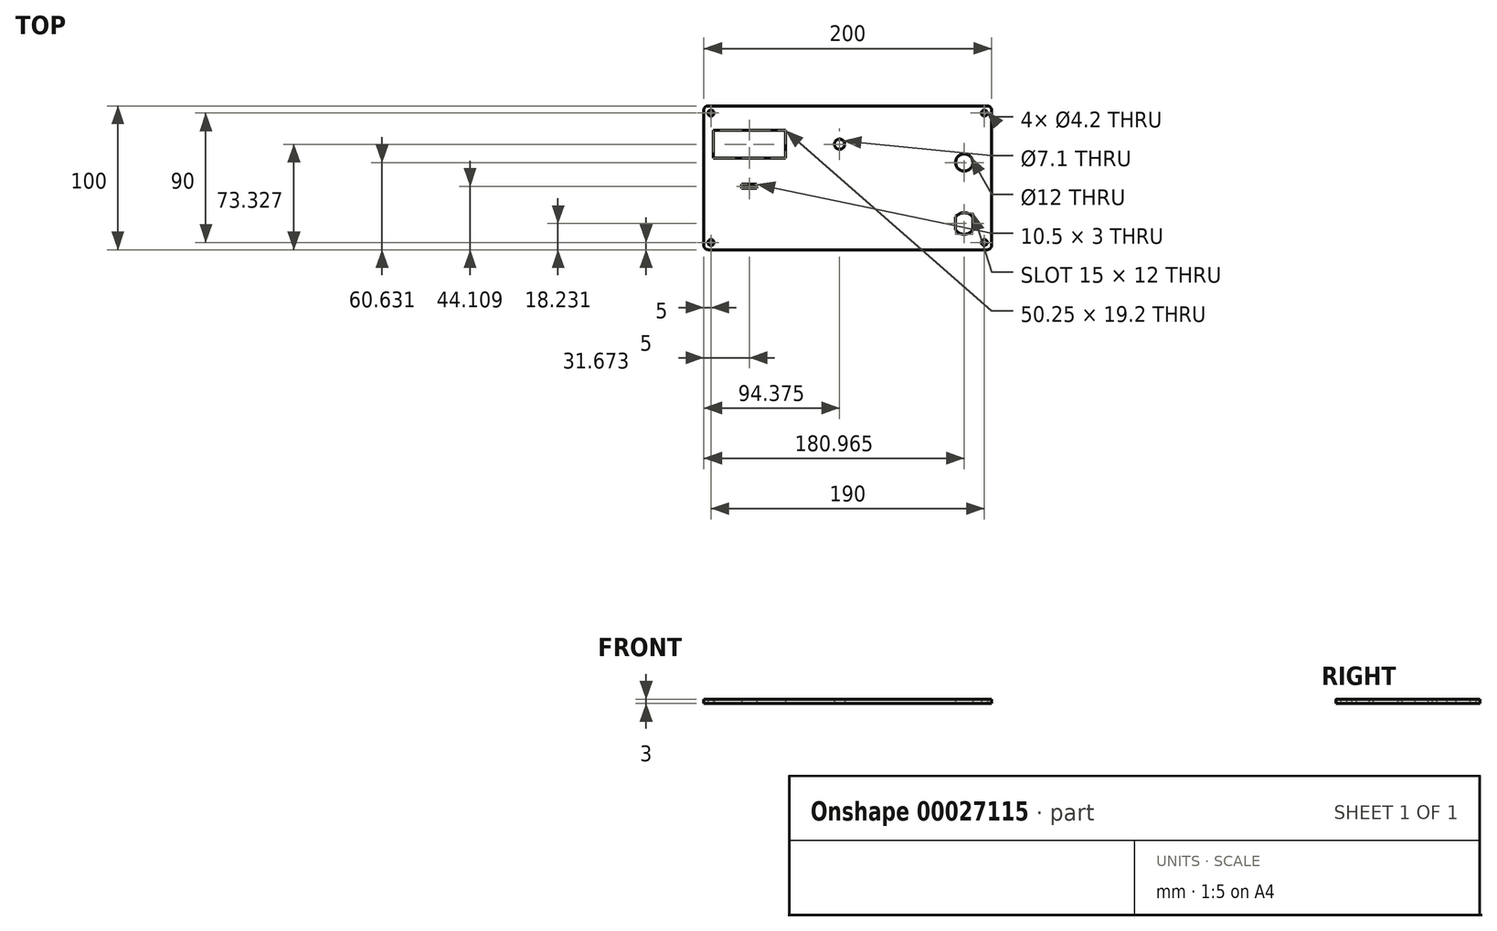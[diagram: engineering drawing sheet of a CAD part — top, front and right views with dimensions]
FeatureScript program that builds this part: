
annotation { "Feature Type Name" : "Feature", "Feature Type Description" : "" }
export const myFeature = defineFeature(function(context is Context, id is Id, definition is map)
    precondition{}
    {
        {
            var Q0;
            Q0=qCreatedBy(makeId("Top.planeOp"),FACE);
            var sketch = newSketch(context, id + "F0", { "sketchPlane" : qUnion([Q0])});
            skLineSegment(sketch, "E0.rect.bottom", {"start": v(100, -50) * mm, "end": v(-100, -50) * mm});
            skLineSegment(sketch, "E0.rect.top", {"start": v(100, 50) * mm, "end": v(-100, 50) * mm});
            skLineSegment(sketch, "E0.rect.left", {"start": v(100, -50) * mm, "end": v(100, 50) * mm});
            skLineSegment(sketch, "E0.rect.right", {"start": v(-100, -50) * mm, "end": v(-100, 50) * mm});
            skPoint(sketch, "E0.rect.middle", {"position": v(0, 0) * mm});
            skLineSegment(sketch, "E1.0", {"start": v(95, 45) * mm, "end": v(-95, 45) * mm, "construction": true});
            skLineSegment(sketch, "E1.1", {"start": v(95, -45) * mm, "end": v(95, 45) * mm, "construction": true});
            skLineSegment(sketch, "E1.2", {"start": v(95, -45) * mm, "end": v(-95, -45) * mm, "construction": true});
            skLineSegment(sketch, "E1.3", {"start": v(-95, -45) * mm, "end": v(-95, 45) * mm, "construction": true});
            skCircle(sketch, "E2", {"center": v(-95, 45) * mm, "radius": 2.1 * mm});
            skCircle(sketch, "E3.MirrorC", {"center": v(95, -45) * mm, "radius": 2.1 * mm});
            skLineSegment(sketch, "E4.bottom", {"start": v(-93.45, 32.93) * mm, "end": v(-43.2, 32.93) * mm});
            skLineSegment(sketch, "E4.top", {"start": v(-93.45, 13.73) * mm, "end": v(-43.2, 13.73) * mm});
            skLineSegment(sketch, "E4.left", {"start": v(-93.45, 32.93) * mm, "end": v(-93.45, 13.73) * mm});
            skLineSegment(sketch, "E4.right", {"start": v(-43.2, 32.93) * mm, "end": v(-43.2, 13.73) * mm});
            skLineSegment(sketch, "E5", {"start": v(-68.33, 32.93) * mm, "end": v(-68.33, 13.73) * mm, "construction": true});
            skLineSegment(sketch, "E6", {"start": v(-93.45, 23.33) * mm, "end": v(-43.2, 23.33) * mm, "construction": true});
            skLineSegment(sketch, "E7.rect.bottom", {"start": v(-43.2, 36.83) * mm, "end": v(-93.45, 36.83) * mm, "construction": true});
            skLineSegment(sketch, "E7.rect.top", {"start": v(-43.2, 9.83) * mm, "end": v(-93.45, 9.83) * mm, "construction": true});
            skLineSegment(sketch, "E7.rect.left", {"start": v(-43.2, 36.83) * mm, "end": v(-43.2, 9.83) * mm, "construction": true});
            skLineSegment(sketch, "E7.rect.right", {"start": v(-93.45, 36.83) * mm, "end": v(-93.45, 9.83) * mm, "construction": true});
            skPoint(sketch, "E7.rect.middle", {"position": v(-68.33, 23.33) * mm});
            skLineSegment(sketch, "E8.rect.bottom", {"start": v(-50.43, -4.4) * mm, "end": v(-86.23, -4.4) * mm, "construction": true});
            skLineSegment(sketch, "E8.rect.top", {"start": v(-50.43, -36.4) * mm, "end": v(-86.23, -36.4) * mm, "construction": true});
            skLineSegment(sketch, "E8.rect.left", {"start": v(-50.43, -4.4) * mm, "end": v(-50.43, -36.4) * mm, "construction": true});
            skLineSegment(sketch, "E8.rect.right", {"start": v(-86.23, -4.4) * mm, "end": v(-86.23, -36.4) * mm, "construction": true});
            skPoint(sketch, "E8.rect.middle", {"position": v(-68.33, -20.4) * mm});
            skLineSegment(sketch, "E9.rect.bottom", {"start": v(-63.08, -7.4) * mm, "end": v(-73.58, -7.4) * mm});
            skLineSegment(sketch, "E9.rect.left", {"start": v(-63.08, -7.4) * mm, "end": v(-63.08, -4.4) * mm});
            skLineSegment(sketch, "E9.rect.right", {"start": v(-73.58, -7.4) * mm, "end": v(-73.58, -4.4) * mm});
            skPoint(sketch, "E9.rect.middle", {"position": v(-68.33, -4.4) * mm});
            skLineSegment(sketch, "E10", {"start": v(-73.58, -4.4) * mm, "end": v(-63.08, -4.4) * mm});
            skPoint(sketch, "E11.orphan", {"position": v(-63.08, -1.4) * mm});
            skPoint(sketch, "E12.orphan", {"position": v(-73.58, -1.4) * mm});
            skCircle(sketch, "E13", {"center": v(-5.63, 23.33) * mm, "radius": 3.55 * mm});
            skCircle(sketch, "E14", {"center": v(-5.63, 23.33) * mm, "radius": 9.25 * mm, "construction": true});
            skArc(sketch, "E15", {"start": v(74.97, -36.27) * mm, "mid": v(80.97, -39.27) * mm, "end": v(86.97, -36.27) * mm});
            skLineSegment(sketch, "E16", {"start": v(86.97, -27.27) * mm, "end": v(86.97, -36.27) * mm});
            skLineSegment(sketch, "E17", {"start": v(80.97, -24.27) * mm, "end": v(80.97, -39.27) * mm, "construction": true});
            skLineSegment(sketch, "E18.MirrorCS", {"start": v(74.97, -27.27) * mm, "end": v(74.97, -36.27) * mm});
            skArc(sketch, "E19.trimOffspring", {"start": v(86.97, -27.27) * mm, "mid": v(80.97, -24.27) * mm, "end": v(74.97, -27.27) * mm});
            skLineSegment(sketch, "E20.rect.bottom", {"start": v(90.47, -2.37) * mm, "end": v(71.47, -2.37) * mm, "construction": true});
            skLineSegment(sketch, "E20.rect.top", {"start": v(90.47, 38.63) * mm, "end": v(71.47, 38.63) * mm, "construction": true});
            skLineSegment(sketch, "E20.rect.left", {"start": v(90.47, -2.37) * mm, "end": v(90.47, 38.63) * mm, "construction": true});
            skLineSegment(sketch, "E20.rect.right", {"start": v(71.47, -2.37) * mm, "end": v(71.47, 38.63) * mm, "construction": true});
            skPoint(sketch, "E20.rect.middle", {"position": v(80.97, 18.13) * mm});
            skLineSegment(sketch, "E21", {"start": v(71.47, 23.63) * mm, "end": v(90.47, 23.63) * mm, "construction": true});
            skCircle(sketch, "E22", {"center": v(80.97, 10.63) * mm, "radius": 6 * mm});
            skCircle(sketch, "E23.MirrorC", {"center": v(95, 45) * mm, "radius": 2.1 * mm});
            skCircle(sketch, "E24.MirrorC", {"center": v(-95, -45) * mm, "radius": 2.1 * mm});
            skSolve(sketch);
        }
        {
            var Q0;
            Q0=makeQuery(id+"F0.imprint","IMPRINT",FACE,{"disambiguationData":[TD([[makeQuery(id+"F0.imprint","IMPRINT",EDGE,{"derivedFrom":sQuery(id+"F0.wireOp",EDGE,"E0.rect.bottom")}),-1.0]])]});
            extrude(context, id + "F1", {"entities" : qUnion([Q0]), "depth" : 3 * mm});
        }
        {
            var Q0;
            Q0=makeQuery(id+"F1.opExtrude","SWEPT_EDGE",EDGE,{"disambiguationData":[OSD([sQuery(id+"F0.wireOp",EDGE,"E0.rect.top"),sQuery(id+"F0.wireOp",EDGE,"E0.rect.left")])]});
            var Q1;
            Q1=makeQuery(id+"F1.opExtrude","SWEPT_EDGE",EDGE,{"disambiguationData":[OSD([sQuery(id+"F0.wireOp",EDGE,"E0.rect.bottom"),sQuery(id+"F0.wireOp",EDGE,"E0.rect.left")])]});
            var Q2;
            Q2=makeQuery(id+"F1.opExtrude","SWEPT_EDGE",EDGE,{"disambiguationData":[OSD([sQuery(id+"F0.wireOp",EDGE,"E0.rect.bottom"),sQuery(id+"F0.wireOp",EDGE,"E0.rect.right")])]});
            var Q3;
            Q3=makeQuery(id+"F1.opExtrude","SWEPT_EDGE",EDGE,{"disambiguationData":[OSD([sQuery(id+"F0.wireOp",EDGE,"E0.rect.top"),sQuery(id+"F0.wireOp",EDGE,"E0.rect.right")])]});
            fillet(context, id + "F2", {"entities" : qUnion([Q0, Q1, Q2, Q3]), "radius" : 3 * mm, "tangentPropagation" : true, "allowEdgeOverflow" : false});
        }
    });
